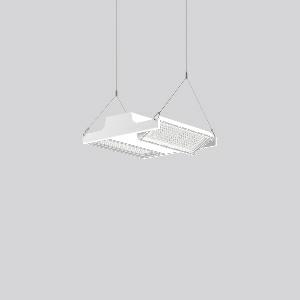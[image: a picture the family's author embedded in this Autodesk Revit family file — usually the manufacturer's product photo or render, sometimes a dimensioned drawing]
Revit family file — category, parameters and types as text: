
# Revit family: light_case_921680_002_76_e213
name_source: partatom
category: Lighting Fixtures
units: mm (PartAtom-declared; Revit-internal decimal feet)

## family parameters
Cut with Voids When Loaded = No
Host = Face
Light Source = No
Part Type = Normal
Room Calculation Point = No
Round Connector Dimension = Use Diameter
Shared = No

## types (1)
- LIGHT CASE (1 x LED Modul 840, 8850 lm, 4000)
    Apparent Load = 117 VA
    CIE Flux Codes = 89 96 99 100 100
    Color Rendering = 80
    Color Temperature = 4000
    Default Elevation = 1800 mm
    Description = Series: LIGHT CASE
Flat highbay luminaire for chain or cable suspension with 2 LED modules that can be swivelled. Housing: die cast aluminium and sheet steel, powder-coated. Optimised thermal management thanks to special luminaire design. Self-cleaning heat sink for constant heat dissipation. Cover: plastic (polycarbonate, shockproof), with integrated four-row lens system. LED modules can be swivelled ± 30° for optimum illumination. Suitable for chain or steel cable suspension (to be provided on site). With 5-pin connection terminal (1.5 m). With integrated movement sensor and light sensor for daylight detection on request. Ball impact proof in accordance with DIN 18032-03 (except steel cable suspension). Luminaire with limited surface temperature in accordance with EN 60598-2-24 for use in environments in which a deposit of conductive dust on the luminaire can be expected. 
Colour: white
Length: 406 mm
Width: 397 mm
Height: 110 mm
Lamp: LED
Socket: without socket
Colour temperature: 4000K
Colour rendering index (CRI): 80
System power: 117 W
Rated luminous flux: 17700 lm
Luminous efficiency: 151 lm/W
Control gear: Converter, dimmable, DALI
Protection class: I
Type of protection: IP 65
    Height = 110 mm
    Lamp = 1 x LED Modul 840
    Lamp Light Flux = 8850 lm
    Lamp count = 1
    Length = 406 mm
    Lifetime = 50000 h
    Luminous efficacy = 151 lm/W
    Manufacturer = RZB
    ModVariant = No
    Model = 921680.002.76
    Mounting Place = Ceiling
    Mounting Type = Pendant
    Number of Poles = 1
    OnlyDefault = Yes
    Power Factor = 1
    Product Name = LIGHT CASE
    Product group = Pendant commercial luminaires
    ProductGroupID = 903
    Protection Class = Protection class I
    Protection Degree = IP 65
    RLX_Detail_Level = 1
    RLX_Emergency_Light_Flux = 0 lm
    RLX_Emergency_Type = 0
    RLX_Emergency_Type_DB = No
    RlxData = <blob elided: 25917 chars, md5=61f9dbd5>
    Socket = socket
    Standby Power = 0 W
    System Light Flux = 17700 lm
    System Power = 117 W
    Type Comments = Product without accessories
    Type Image = 921517.002.76.jpg
    URL = http://relux.com
    VarID = ---
    Voltage = 230 V
    Voltage Range = 220-240 V
    Weight = 0.00 kg
    Width = 397 mm

## geometry (parser evidence)
native form markers: Blend x4, Sweep x16
no freeform markers — native parametric forms only
